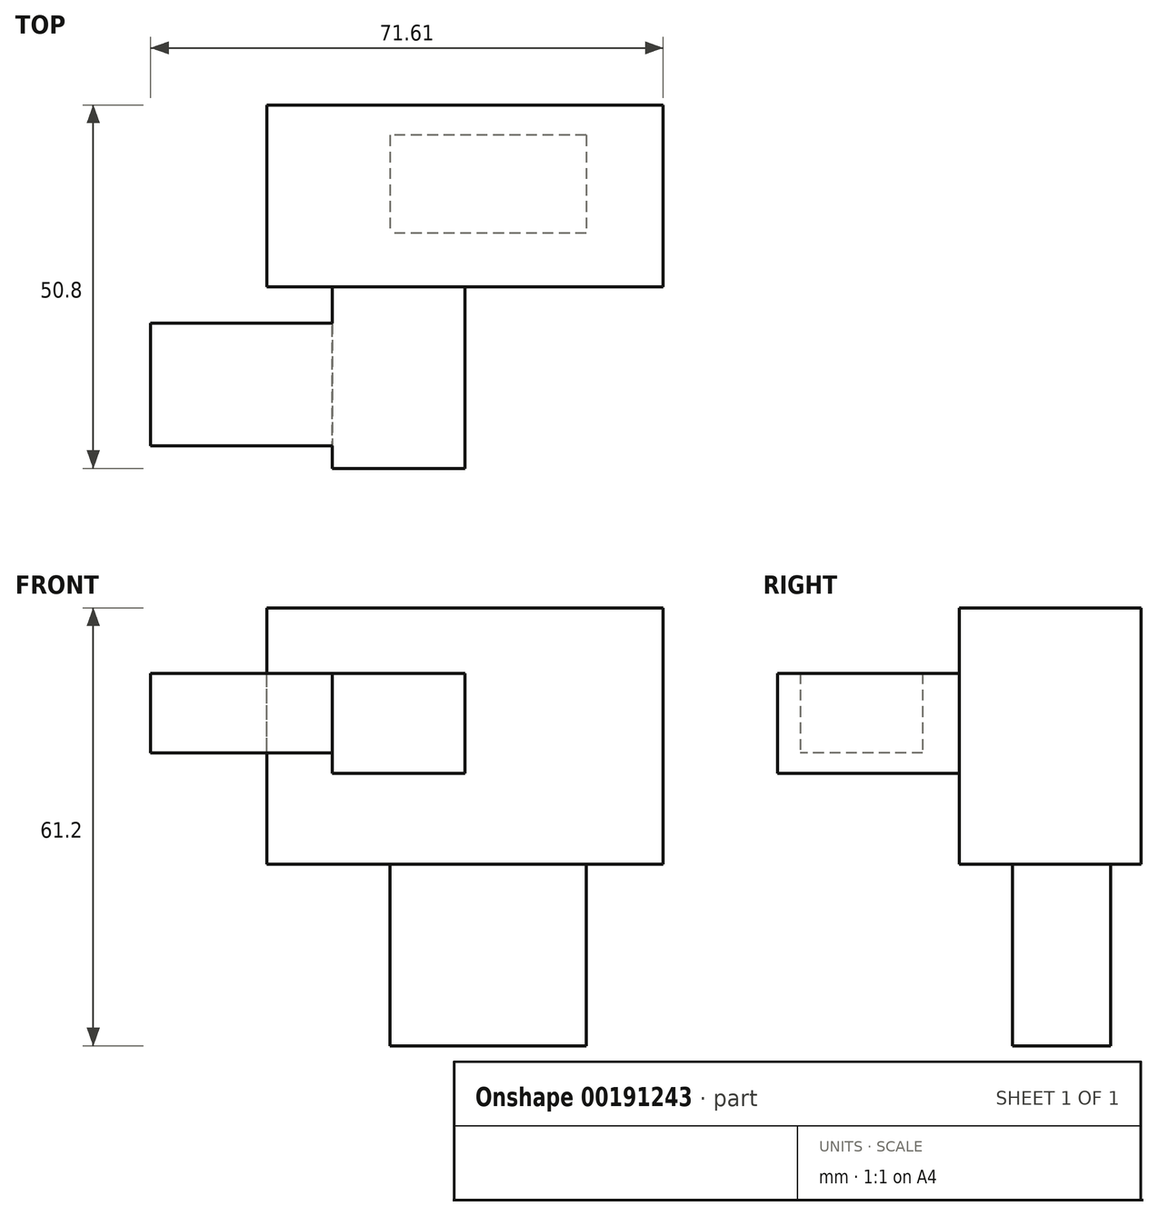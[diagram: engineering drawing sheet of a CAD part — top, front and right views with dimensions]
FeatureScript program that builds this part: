
annotation { "Feature Type Name" : "Feature", "Feature Type Description" : "" }
export const myFeature = defineFeature(function(context is Context, id is Id, definition is map)
    precondition{}
    {
        {
            var Q0;
            Q0=qCreatedBy(makeId("Front.planeOp"),FACE);
            var sketch = newSketch(context, id + "F0", { "sketchPlane" : qUnion([Q0])});
            skLineSegment(sketch, "E0.bottom", {"start": v(0, 0) * mm, "end": v(55.34, 0) * mm});
            skLineSegment(sketch, "E0.top", {"start": v(0, 35.8) * mm, "end": v(55.34, 35.8) * mm});
            skLineSegment(sketch, "E0.left", {"start": v(0, 0) * mm, "end": v(0, 35.8) * mm});
            skLineSegment(sketch, "E0.right", {"start": v(55.34, 0) * mm, "end": v(55.34, 35.8) * mm});
            skSolve(sketch);
        }
        {
            var Q0;
            Q0=makeQuery(id+"F0.imprint","IMPRINT",FACE,{"disambiguationData":[TD([[makeQuery(id+"F0.imprint","IMPRINT",EDGE,{"derivedFrom":sQuery(id+"F0.wireOp",EDGE,"E0.bottom")}),1.0]])]});
            extrude(context, id + "F1", {"entities" : qUnion([Q0]), "depth" : 25.4 * mm});
        }
        {
            var Q0;
            Q0=makeQuery(id+"F1.opExtrude","CAP_FACE",FACE,{"disambiguationData":[OSD([sQuery(id+"F0.wireOp",EDGE,"E0.bottom"),sQuery(id+"F0.wireOp",EDGE,"E0.top"),sQuery(id+"F0.wireOp",EDGE,"E0.left"),sQuery(id+"F0.wireOp",EDGE,"E0.right")])],"isStart":false});
            var sketch = newSketch(context, id + "F2", { "sketchPlane" : qUnion([Q0])});
            skLineSegment(sketch, "E1.bottom", {"start": v(9.13, 26.67) * mm, "end": v(27.67, 26.67) * mm});
            skLineSegment(sketch, "E1.top", {"start": v(9.13, 12.7) * mm, "end": v(27.67, 12.7) * mm});
            skLineSegment(sketch, "E1.left", {"start": v(9.13, 26.67) * mm, "end": v(9.13, 12.7) * mm});
            skLineSegment(sketch, "E1.right", {"start": v(27.67, 26.67) * mm, "end": v(27.67, 12.7) * mm});
            skSolve(sketch);
        }
        {
            var Q0;
            Q0=makeQuery(id+"F2.imprint","IMPRINT",FACE,{"disambiguationData":[TD([[makeQuery(id+"F2.imprint","IMPRINT",EDGE,{"derivedFrom":sQuery(id+"F2.wireOp",EDGE,"E1.bottom")}),-1.0]])]});
            extrude(context, id + "F3", {"entities" : qUnion([Q0]), "operationType" : NewBodyOperationType.ADD, "depth" : 25.4 * mm});
        }
        {
            var Q0;
            Q0=makeQuery(id+"F3.opExtrude","SWEPT_FACE",FACE,{"disambiguationData":[OSD([sQuery(id+"F2.wireOp",EDGE,"E1.left")])]});
            var sketch = newSketch(context, id + "F4", { "sketchPlane" : qUnion([Q0])});
            skLineSegment(sketch, "E2.bottom", {"start": v(30.52, 26.67) * mm, "end": v(47.64, 26.67) * mm});
            skLineSegment(sketch, "E2.top", {"start": v(30.52, 15.55) * mm, "end": v(47.64, 15.55) * mm});
            skLineSegment(sketch, "E2.left", {"start": v(30.52, 26.67) * mm, "end": v(30.52, 15.55) * mm});
            skLineSegment(sketch, "E2.right", {"start": v(47.64, 26.67) * mm, "end": v(47.64, 15.55) * mm});
            skSolve(sketch);
        }
        {
            var Q0;
            Q0=makeQuery(id+"F4.imprint","IMPRINT",FACE,{"disambiguationData":[TD([[makeQuery(id+"F4.imprint","IMPRINT",EDGE,{"derivedFrom":sQuery(id+"F4.wireOp",EDGE,"E2.bottom")}),1.0]])]});
            extrude(context, id + "F5", {"entities" : qUnion([Q0]), "operationType" : NewBodyOperationType.ADD, "depth" : 25.4 * mm});
        }
        {
            var Q0;
            Q0=makeQuery(id+"F1.opExtrude","SWEPT_FACE",FACE,{"disambiguationData":[OSD([sQuery(id+"F0.wireOp",EDGE,"E0.bottom")])]});
            var sketch = newSketch(context, id + "F6", { "sketchPlane" : qUnion([Q0])});
            skLineSegment(sketch, "E3.bottom", {"start": v(44.6, 4.24) * mm, "end": v(17.16, 4.24) * mm});
            skLineSegment(sketch, "E3.top", {"start": v(44.6, 17.95) * mm, "end": v(17.16, 17.95) * mm});
            skLineSegment(sketch, "E3.left", {"start": v(44.6, 4.24) * mm, "end": v(44.6, 17.95) * mm});
            skLineSegment(sketch, "E3.right", {"start": v(17.16, 4.24) * mm, "end": v(17.16, 17.95) * mm});
            skSolve(sketch);
        }
        {
            var Q0;
            Q0=makeQuery(id+"F6.imprint","IMPRINT",FACE,{"disambiguationData":[TD([[makeQuery(id+"F6.imprint","IMPRINT",EDGE,{"derivedFrom":sQuery(id+"F6.wireOp",EDGE,"E3.bottom")}),-1.0]])]});
            extrude(context, id + "F7", {"entities" : qUnion([Q0]), "operationType" : NewBodyOperationType.ADD, "depth" : 25.4 * mm});
        }
    });
